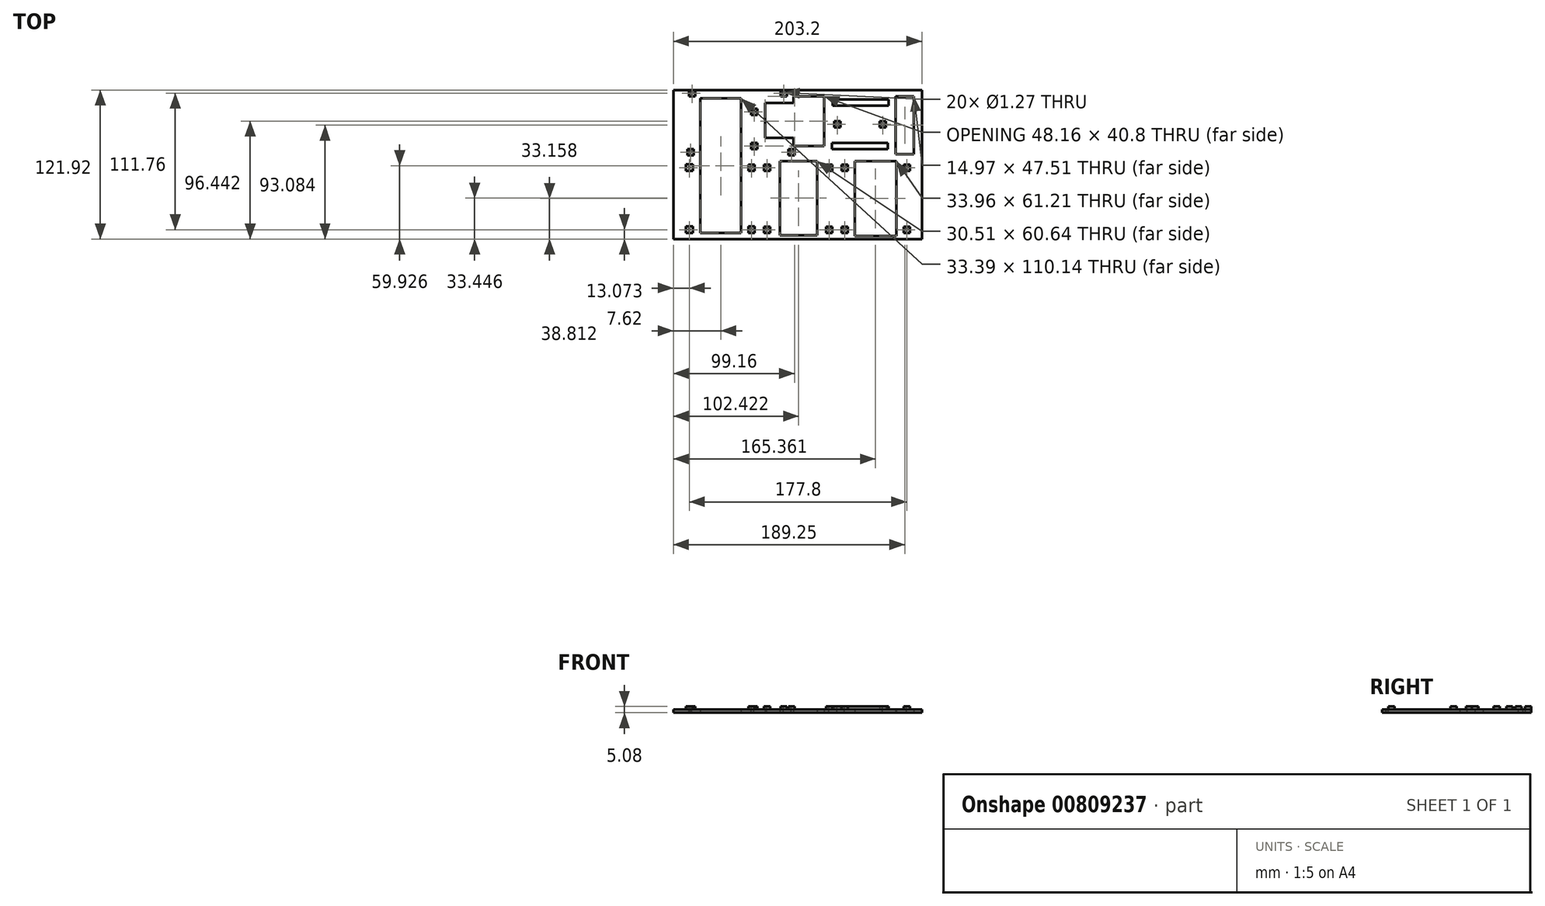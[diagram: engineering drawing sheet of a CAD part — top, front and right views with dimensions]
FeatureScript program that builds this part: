
annotation { "Feature Type Name" : "Feature", "Feature Type Description" : "" }
export const myFeature = defineFeature(function(context is Context, id is Id, definition is map)
    precondition{}
    {
        {
            var Q0;
            Q0=qCreatedBy(makeId("Top.planeOp"),FACE);
            var sketch = newSketch(context, id + "F0", { "sketchPlane" : qUnion([Q0])});
            skLineSegment(sketch, "E0.bottom", {"start": v(101.6, 60.96) * mm, "end": v(-101.6, 60.96) * mm});
            skLineSegment(sketch, "E0.top", {"start": v(101.6, -60.96) * mm, "end": v(-101.6, -60.96) * mm});
            skLineSegment(sketch, "E0.left", {"start": v(101.6, 60.96) * mm, "end": v(101.6, -60.96) * mm});
            skLineSegment(sketch, "E0.right", {"start": v(-101.6, 60.96) * mm, "end": v(-101.6, -60.96) * mm});
            skPoint(sketch, "E0.middle", {"position": v(0, 0) * mm});
            skLineSegment(sketch, "E1.bottom", {"start": v(-8.9, 55.88) * mm, "end": v(-13.97, 55.88) * mm});
            skLineSegment(sketch, "E1.top", {"start": v(-8.9, 60.96) * mm, "end": v(-13.97, 60.96) * mm});
            skLineSegment(sketch, "E1.left", {"start": v(-8.9, 55.88) * mm, "end": v(-8.9, 60.96) * mm});
            skLineSegment(sketch, "E1.right", {"start": v(-13.97, 55.88) * mm, "end": v(-13.97, 60.96) * mm});
            skPoint(sketch, "E1.middle", {"position": v(-11.43, 58.42) * mm});
            skLineSegment(sketch, "E2.bottom", {"start": v(-83.82, 55.88) * mm, "end": v(-88.9, 55.88) * mm});
            skLineSegment(sketch, "E2.top", {"start": v(-83.82, 60.96) * mm, "end": v(-88.9, 60.96) * mm});
            skLineSegment(sketch, "E2.left", {"start": v(-83.82, 55.88) * mm, "end": v(-83.82, 60.96) * mm});
            skLineSegment(sketch, "E2.right", {"start": v(-88.9, 55.88) * mm, "end": v(-88.9, 60.96) * mm});
            skPoint(sketch, "E2.middle", {"position": v(-86.36, 58.42) * mm});
            skLineSegment(sketch, "E3.bottom", {"start": v(-85.1, 7.62) * mm, "end": v(-90.17, 7.62) * mm});
            skLineSegment(sketch, "E3.top", {"start": v(-85.1, 12.7) * mm, "end": v(-90.17, 12.7) * mm});
            skLineSegment(sketch, "E3.left", {"start": v(-85.1, 7.62) * mm, "end": v(-85.1, 12.7) * mm});
            skLineSegment(sketch, "E3.right", {"start": v(-90.17, 7.62) * mm, "end": v(-90.17, 12.7) * mm});
            skPoint(sketch, "E3.middle", {"position": v(-87.63, 10.16) * mm});
            skLineSegment(sketch, "E4.bottom", {"start": v(-2.54, 7.62) * mm, "end": v(-7.62, 7.62) * mm});
            skLineSegment(sketch, "E4.top", {"start": v(-2.54, 12.7) * mm, "end": v(-7.62, 12.7) * mm});
            skLineSegment(sketch, "E4.left", {"start": v(-2.54, 7.62) * mm, "end": v(-2.54, 12.7) * mm});
            skLineSegment(sketch, "E4.right", {"start": v(-7.62, 7.62) * mm, "end": v(-7.62, 12.7) * mm});
            skPoint(sketch, "E4.middle", {"position": v(-5.08, 10.16) * mm});
            skLineSegment(sketch, "E5.bottom", {"start": v(-33.02, 40.64) * mm, "end": v(-38.1, 40.64) * mm});
            skLineSegment(sketch, "E5.top", {"start": v(-33.02, 45.72) * mm, "end": v(-38.1, 45.72) * mm});
            skLineSegment(sketch, "E5.left", {"start": v(-33.02, 40.64) * mm, "end": v(-33.02, 45.72) * mm});
            skLineSegment(sketch, "E5.right", {"start": v(-38.1, 40.64) * mm, "end": v(-38.1, 45.72) * mm});
            skPoint(sketch, "E5.middle", {"position": v(-35.56, 43.18) * mm});
            skLineSegment(sketch, "E6.bottom", {"start": v(-33.02, 12.7) * mm, "end": v(-38.1, 12.7) * mm});
            skLineSegment(sketch, "E6.top", {"start": v(-33.02, 17.78) * mm, "end": v(-38.1, 17.78) * mm});
            skLineSegment(sketch, "E6.left", {"start": v(-33.02, 12.7) * mm, "end": v(-33.02, 17.78) * mm});
            skLineSegment(sketch, "E6.right", {"start": v(-38.1, 12.7) * mm, "end": v(-38.1, 17.78) * mm});
            skPoint(sketch, "E6.middle", {"position": v(-35.56, 15.24) * mm});
            skPoint(sketch, "E7.middle", {"position": v(-88.53, -53.34) * mm});
            skLineSegment(sketch, "E8.bottom", {"start": v(-85.61, -5.1) * mm, "end": v(-91.44, -5.1) * mm});
            skLineSegment(sketch, "E8.top", {"start": v(-85.61, 0.02) * mm, "end": v(-91.44, 0.02) * mm});
            skLineSegment(sketch, "E8.left", {"start": v(-85.61, -5.1) * mm, "end": v(-85.61, 0.02) * mm});
            skLineSegment(sketch, "E8.right", {"start": v(-91.44, -5.1) * mm, "end": v(-91.44, 0.02) * mm});
            skPoint(sketch, "E8.middle", {"position": v(-88.53, -2.54) * mm});
            skLineSegment(sketch, "E9.bottom", {"start": v(-35.19, 0) * mm, "end": v(-40.27, 0) * mm});
            skLineSegment(sketch, "E9.top", {"start": v(-35.19, -5.08) * mm, "end": v(-40.27, -5.08) * mm});
            skLineSegment(sketch, "E9.left", {"start": v(-35.19, 0) * mm, "end": v(-35.19, -5.08) * mm});
            skLineSegment(sketch, "E9.right", {"start": v(-40.27, 0) * mm, "end": v(-40.27, -5.08) * mm});
            skPoint(sketch, "E9.middle", {"position": v(-37.73, -2.54) * mm});
            skLineSegment(sketch, "E10.bottom", {"start": v(-40.27, -50.78) * mm, "end": v(-35.19, -50.78) * mm});
            skLineSegment(sketch, "E10.top", {"start": v(-40.27, -55.9) * mm, "end": v(-35.19, -55.9) * mm});
            skLineSegment(sketch, "E10.left", {"start": v(-40.27, -50.78) * mm, "end": v(-40.27, -55.9) * mm});
            skLineSegment(sketch, "E10.right", {"start": v(-35.19, -50.78) * mm, "end": v(-35.19, -55.9) * mm});
            skPoint(sketch, "E10.middle", {"position": v(-37.73, -53.34) * mm});
            skLineSegment(sketch, "E11.bottom", {"start": v(-85.61, -50.78) * mm, "end": v(-91.44, -50.75) * mm});
            skLineSegment(sketch, "E11.left", {"start": v(-85.61, -50.78) * mm, "end": v(-85.61, -55.93) * mm});
            skLineSegment(sketch, "E11.right", {"start": v(-91.44, -50.75) * mm, "end": v(-91.44, -55.9) * mm});
            skLineSegment(sketch, "E12", {"start": v(-91.44, -55.9) * mm, "end": v(-85.61, -55.93) * mm});
            skLineSegment(sketch, "E13.bottom", {"start": v(-22.49, -55.88) * mm, "end": v(-27.57, -55.88) * mm});
            skLineSegment(sketch, "E13.top", {"start": v(-22.49, -50.8) * mm, "end": v(-27.57, -50.8) * mm});
            skLineSegment(sketch, "E13.left", {"start": v(-22.49, -55.88) * mm, "end": v(-22.49, -50.8) * mm});
            skLineSegment(sketch, "E13.right", {"start": v(-27.57, -55.88) * mm, "end": v(-27.57, -50.8) * mm});
            skPoint(sketch, "E13.middle", {"position": v(-25.03, -53.34) * mm});
            skLineSegment(sketch, "E14.bottom", {"start": v(28.31, -50.8) * mm, "end": v(23.23, -50.8) * mm});
            skLineSegment(sketch, "E14.top", {"start": v(28.31, -55.88) * mm, "end": v(23.23, -55.88) * mm});
            skLineSegment(sketch, "E14.left", {"start": v(28.31, -50.8) * mm, "end": v(28.31, -55.88) * mm});
            skLineSegment(sketch, "E14.right", {"start": v(23.23, -50.8) * mm, "end": v(23.23, -55.88) * mm});
            skPoint(sketch, "E14.middle", {"position": v(25.77, -53.34) * mm});
            skLineSegment(sketch, "E15.bottom", {"start": v(23.23, -5.08) * mm, "end": v(28.31, -5.08) * mm});
            skLineSegment(sketch, "E15.top", {"start": v(23.23, 0) * mm, "end": v(28.31, 0) * mm});
            skLineSegment(sketch, "E15.left", {"start": v(23.23, -5.08) * mm, "end": v(23.23, 0) * mm});
            skLineSegment(sketch, "E15.right", {"start": v(28.31, -5.08) * mm, "end": v(28.31, 0) * mm});
            skPoint(sketch, "E15.middle", {"position": v(25.77, -2.54) * mm});
            skLineSegment(sketch, "E16.bottom", {"start": v(-27.57, -5.08) * mm, "end": v(-22.49, -5.08) * mm});
            skLineSegment(sketch, "E16.top", {"start": v(-27.57, 0) * mm, "end": v(-22.49, 0) * mm});
            skLineSegment(sketch, "E16.left", {"start": v(-27.57, -5.08) * mm, "end": v(-27.57, 0) * mm});
            skLineSegment(sketch, "E16.right", {"start": v(-22.49, -5.08) * mm, "end": v(-22.49, 0) * mm});
            skPoint(sketch, "E16.middle", {"position": v(-25.03, -2.54) * mm});
            skPoint(sketch, "E16.middle.positionSnap0", {"position": v(-25.03, -50.8) * mm});
            skPoint(sketch, "E16.centerSnap0", {"position": v(-25.03, -50.8) * mm});
            skLineSegment(sketch, "E17.bottom", {"start": v(41.01, 0) * mm, "end": v(35.93, 0) * mm});
            skLineSegment(sketch, "E17.top", {"start": v(41.01, -5.08) * mm, "end": v(35.93, -5.08) * mm});
            skLineSegment(sketch, "E17.left", {"start": v(41.01, 0) * mm, "end": v(41.01, -5.08) * mm});
            skLineSegment(sketch, "E17.right", {"start": v(35.93, 0) * mm, "end": v(35.93, -5.08) * mm});
            skPoint(sketch, "E17.middle", {"position": v(38.47, -2.54) * mm});
            skLineSegment(sketch, "E18.bottom", {"start": v(91.81, 0) * mm, "end": v(86.73, 0) * mm});
            skLineSegment(sketch, "E18.top", {"start": v(91.81, -5.08) * mm, "end": v(86.73, -5.08) * mm});
            skLineSegment(sketch, "E18.left", {"start": v(91.81, 0) * mm, "end": v(91.81, -5.08) * mm});
            skLineSegment(sketch, "E18.right", {"start": v(86.73, 0) * mm, "end": v(86.73, -5.08) * mm});
            skPoint(sketch, "E18.middle", {"position": v(89.27, -2.54) * mm});
            skLineSegment(sketch, "E19.bottom", {"start": v(41.01, -50.8) * mm, "end": v(35.93, -50.8) * mm});
            skLineSegment(sketch, "E19.top", {"start": v(41.01, -55.88) * mm, "end": v(35.93, -55.88) * mm});
            skLineSegment(sketch, "E19.left", {"start": v(41.01, -50.8) * mm, "end": v(41.01, -55.88) * mm});
            skLineSegment(sketch, "E19.right", {"start": v(35.93, -50.8) * mm, "end": v(35.93, -55.88) * mm});
            skPoint(sketch, "E19.middle", {"position": v(38.47, -53.34) * mm});
            skLineSegment(sketch, "E20.bottom", {"start": v(86.73, -50.8) * mm, "end": v(91.81, -50.8) * mm});
            skLineSegment(sketch, "E20.top", {"start": v(86.73, -55.88) * mm, "end": v(91.81, -55.88) * mm});
            skLineSegment(sketch, "E20.left", {"start": v(86.73, -50.8) * mm, "end": v(86.73, -55.88) * mm});
            skLineSegment(sketch, "E20.right", {"start": v(91.81, -50.8) * mm, "end": v(91.81, -55.88) * mm});
            skPoint(sketch, "E20.middle", {"position": v(89.27, -53.34) * mm});
            skLineSegment(sketch, "E21.bottom", {"start": v(35.02, 30.3) * mm, "end": v(29.94, 30.3) * mm});
            skLineSegment(sketch, "E21.top", {"start": v(35.02, 35.38) * mm, "end": v(29.94, 35.38) * mm});
            skLineSegment(sketch, "E21.left", {"start": v(35.02, 30.3) * mm, "end": v(35.02, 35.38) * mm});
            skLineSegment(sketch, "E21.right", {"start": v(29.94, 30.3) * mm, "end": v(29.94, 35.38) * mm});
            skPoint(sketch, "E21.middle", {"position": v(32.48, 32.84) * mm});
            skLineSegment(sketch, "E22.bottom", {"start": v(72.1, 35.38) * mm, "end": v(67.02, 35.38) * mm});
            skLineSegment(sketch, "E22.top", {"start": v(72.1, 30.3) * mm, "end": v(67.02, 30.3) * mm});
            skLineSegment(sketch, "E22.left", {"start": v(72.1, 35.38) * mm, "end": v(72.1, 30.3) * mm});
            skLineSegment(sketch, "E22.right", {"start": v(67.02, 35.38) * mm, "end": v(67.02, 30.3) * mm});
            skPoint(sketch, "E22.middle", {"position": v(69.56, 32.84) * mm});
            skLineSegment(sketch, "E23.bottom", {"start": v(74.44, 53.16) * mm, "end": v(28.72, 53.16) * mm});
            skLineSegment(sketch, "E23.top", {"start": v(74.44, 48.08) * mm, "end": v(28.72, 48.08) * mm});
            skLineSegment(sketch, "E23.left", {"start": v(74.44, 53.16) * mm, "end": v(74.44, 48.08) * mm});
            skLineSegment(sketch, "E23.right", {"start": v(28.72, 53.16) * mm, "end": v(28.72, 48.08) * mm});
            skPoint(sketch, "E23.middle", {"position": v(51.58, 50.62) * mm});
            skLineSegment(sketch, "E24.bottom", {"start": v(73.88, 17.6) * mm, "end": v(28.16, 17.6) * mm});
            skLineSegment(sketch, "E24.top", {"start": v(73.88, 12.52) * mm, "end": v(28.16, 12.52) * mm});
            skLineSegment(sketch, "E24.left", {"start": v(73.88, 17.6) * mm, "end": v(73.88, 12.52) * mm});
            skLineSegment(sketch, "E24.right", {"start": v(28.16, 17.6) * mm, "end": v(28.16, 12.52) * mm});
            skPoint(sketch, "E24.middle", {"position": v(51.02, 15.06) * mm});
            skLineSegment(sketch, "E25.bottom", {"start": v(-79.48, 54.04) * mm, "end": v(-46.1, 54.04) * mm});
            skLineSegment(sketch, "E25.top", {"start": v(-79.48, -56.1) * mm, "end": v(-46.1, -56.1) * mm});
            skLineSegment(sketch, "E25.left", {"start": v(-79.48, 54.04) * mm, "end": v(-79.48, -56.1) * mm});
            skLineSegment(sketch, "E25.right", {"start": v(-46.1, 54.04) * mm, "end": v(-46.1, -56.1) * mm});
            skLineSegment(sketch, "E26.bottom", {"start": v(-14.43, 2.8) * mm, "end": v(16.08, 2.8) * mm});
            skLineSegment(sketch, "E26.top", {"start": v(-14.43, -57.83) * mm, "end": v(16.08, -57.83) * mm});
            skLineSegment(sketch, "E26.left", {"start": v(-14.43, 2.8) * mm, "end": v(-14.43, -57.83) * mm});
            skLineSegment(sketch, "E26.right", {"start": v(16.08, 2.8) * mm, "end": v(16.08, -57.83) * mm});
            skLineSegment(sketch, "E27.bottom", {"start": v(46.78, 2.8) * mm, "end": v(80.74, 2.8) * mm});
            skLineSegment(sketch, "E27.top", {"start": v(46.78, -58.4) * mm, "end": v(80.74, -58.4) * mm});
            skLineSegment(sketch, "E27.left", {"start": v(46.78, 2.8) * mm, "end": v(46.78, -58.4) * mm});
            skLineSegment(sketch, "E27.right", {"start": v(80.74, 2.8) * mm, "end": v(80.74, -58.4) * mm});
            skLineSegment(sketch, "E28.bottom", {"start": v(80.17, 55.88) * mm, "end": v(95.13, 55.88) * mm});
            skLineSegment(sketch, "E28.top", {"start": v(80.17, 8.37) * mm, "end": v(95.13, 8.37) * mm});
            skLineSegment(sketch, "E28.left", {"start": v(80.17, 55.88) * mm, "end": v(80.17, 8.37) * mm});
            skLineSegment(sketch, "E28.right", {"start": v(95.13, 55.88) * mm, "end": v(95.13, 8.37) * mm});
            skLineSegment(sketch, "E29.bottom", {"start": v(-3.5, 55.88) * mm, "end": v(21.64, 55.88) * mm});
            skLineSegment(sketch, "E29.top", {"start": v(-3.5, 15.08) * mm, "end": v(21.64, 15.08) * mm});
            skLineSegment(sketch, "E29.left", {"start": v(-3.5, 55.88) * mm, "end": v(-3.5, 15.08) * mm});
            skLineSegment(sketch, "E29.right", {"start": v(21.64, 55.88) * mm, "end": v(21.64, 15.08) * mm});
            skLineSegment(sketch, "E30.bottom", {"start": v(-26.52, 50.4) * mm, "end": v(-3.5, 50.4) * mm});
            skLineSegment(sketch, "E30.top", {"start": v(-26.52, 21.6) * mm, "end": v(-3.5, 21.6) * mm});
            skLineSegment(sketch, "E30.left", {"start": v(-26.52, 50.4) * mm, "end": v(-26.52, 21.6) * mm});
            skLineSegment(sketch, "E30.right", {"start": v(-3.5, 50.4) * mm, "end": v(-3.5, 21.6) * mm});
            skSolve(sketch);
        }
        {
            var Q0;
            Q0=makeQuery(id+"F0.imprint","IMPRINT",FACE,{"disambiguationData":[TD([[makeQuery(id+"F0.imprint","IMPRINT",EDGE,{"derivedFrom":sQuery(id+"F0.wireOp",EDGE,"E0.top")}),-1.0]])]});
            extrude(context, id + "F1", {"entities" : qUnion([Q0]), "depth" : 2.54 * mm, "offsetDistance" : 25.4 * mm});
        }
        {
            var Q0;
            Q0=makeQuery(id+"F0.imprint","IMPRINT",FACE,{"disambiguationData":[TD([[makeQuery(id+"F0.imprint","IMPRINT",EDGE,{"derivedFrom":sQuery(id+"F0.wireOp",EDGE,"E2.bottom")}),-1.0]])]});
            var Q1;
            Q1=makeQuery(id+"F0.imprint","IMPRINT",FACE,{"disambiguationData":[TD([[makeQuery(id+"F0.imprint","IMPRINT",EDGE,{"derivedFrom":sQuery(id+"F0.wireOp",EDGE,"E5.bottom")}),-1.0]])]});
            var Q2;
            Q2=makeQuery(id+"F0.imprint","IMPRINT",FACE,{"disambiguationData":[TD([[makeQuery(id+"F0.imprint","IMPRINT",EDGE,{"derivedFrom":sQuery(id+"F0.wireOp",EDGE,"E1.bottom")}),-1.0]])]});
            var Q3;
            Q3=makeQuery(id+"F0.imprint","IMPRINT",FACE,{"disambiguationData":[TD([[makeQuery(id+"F0.imprint","IMPRINT",EDGE,{"derivedFrom":sQuery(id+"F0.wireOp",EDGE,"E6.bottom")}),-1.0]])]});
            var Q4;
            Q4=makeQuery(id+"F0.imprint","IMPRINT",FACE,{"disambiguationData":[TD([[makeQuery(id+"F0.imprint","IMPRINT",EDGE,{"derivedFrom":sQuery(id+"F0.wireOp",EDGE,"E4.bottom")}),-1.0]])]});
            var Q5;
            Q5=makeQuery(id+"F0.imprint","IMPRINT",FACE,{"disambiguationData":[TD([[makeQuery(id+"F0.imprint","IMPRINT",EDGE,{"derivedFrom":sQuery(id+"F0.wireOp",EDGE,"E3.bottom")}),-1.0]])]});
            var Q6;
            Q6=makeQuery(id+"F0.imprint","IMPRINT",FACE,{"disambiguationData":[TD([[makeQuery(id+"F0.imprint","IMPRINT",EDGE,{"derivedFrom":sQuery(id+"F0.wireOp",EDGE,"E8.bottom")}),-1.0]])]});
            var Q7;
            Q7=makeQuery(id+"F0.imprint","IMPRINT",FACE,{"disambiguationData":[TD([[makeQuery(id+"F0.imprint","IMPRINT",EDGE,{"derivedFrom":sQuery(id+"F0.wireOp",EDGE,"E9.bottom")}),1.0]])]});
            var Q8;
            Q8=makeQuery(id+"F0.imprint","IMPRINT",FACE,{"disambiguationData":[TD([[makeQuery(id+"F0.imprint","IMPRINT",EDGE,{"derivedFrom":sQuery(id+"F0.wireOp",EDGE,"E10.bottom")}),-1.0]])]});
            var Q9;
            {var subQ4=sQuery(id+"F0.wireOp",EDGE,"E7.top");Q9=makeQuery(id+"F0.imprint","IMPRINT",FACE,{"disambiguationData":[TD([[makeQuery(id+"F0.imprint","IMPRINT",EDGE,{"derivedFrom":subQ4}),-1.0]])]});}
            var Q10;
            Q10=makeQuery(id+"F0.imprint","IMPRINT",FACE,{"disambiguationData":[TD([[makeQuery(id+"F0.imprint","IMPRINT",EDGE,{"derivedFrom":sQuery(id+"F0.wireOp",EDGE,"E16.bottom")}),1.0]])]});
            var Q11;
            Q11=makeQuery(id+"F0.imprint","IMPRINT",FACE,{"disambiguationData":[TD([[makeQuery(id+"F0.imprint","IMPRINT",EDGE,{"derivedFrom":sQuery(id+"F0.wireOp",EDGE,"E15.bottom")}),1.0]])]});
            var Q12;
            Q12=makeQuery(id+"F0.imprint","IMPRINT",FACE,{"disambiguationData":[TD([[makeQuery(id+"F0.imprint","IMPRINT",EDGE,{"derivedFrom":sQuery(id+"F0.wireOp",EDGE,"E17.bottom")}),1.0]])]});
            var Q13;
            Q13=makeQuery(id+"F0.imprint","IMPRINT",FACE,{"disambiguationData":[TD([[makeQuery(id+"F0.imprint","IMPRINT",EDGE,{"derivedFrom":sQuery(id+"F0.wireOp",EDGE,"E18.bottom")}),1.0]])]});
            var Q14;
            Q14=makeQuery(id+"F0.imprint","IMPRINT",FACE,{"disambiguationData":[TD([[makeQuery(id+"F0.imprint","IMPRINT",EDGE,{"derivedFrom":sQuery(id+"F0.wireOp",EDGE,"E20.bottom")}),-1.0]])]});
            var Q15;
            Q15=makeQuery(id+"F0.imprint","IMPRINT",FACE,{"disambiguationData":[TD([[makeQuery(id+"F0.imprint","IMPRINT",EDGE,{"derivedFrom":sQuery(id+"F0.wireOp",EDGE,"E19.bottom")}),1.0]])]});
            var Q16;
            Q16=makeQuery(id+"F0.imprint","IMPRINT",FACE,{"disambiguationData":[TD([[makeQuery(id+"F0.imprint","IMPRINT",EDGE,{"derivedFrom":sQuery(id+"F0.wireOp",EDGE,"E14.bottom")}),1.0]])]});
            var Q17;
            Q17=makeQuery(id+"F0.imprint","IMPRINT",FACE,{"disambiguationData":[TD([[makeQuery(id+"F0.imprint","IMPRINT",EDGE,{"derivedFrom":sQuery(id+"F0.wireOp",EDGE,"E13.bottom")}),-1.0]])]});
            var Q18;
            Q18=makeQuery(id+"F0.imprint","IMPRINT",FACE,{"disambiguationData":[TD([[makeQuery(id+"F0.imprint","IMPRINT",EDGE,{"derivedFrom":sQuery(id+"F0.wireOp",EDGE,"E11.bottom")}),1.0]])]});
            var Q19;
            Q19=makeQuery(id+"F0.imprint","IMPRINT",FACE,{"disambiguationData":[TD([[makeQuery(id+"F0.imprint","IMPRINT",EDGE,{"derivedFrom":sQuery(id+"F0.wireOp",EDGE,"E21.bottom")}),-1.0]])]});
            var Q20;
            Q20=makeQuery(id+"F0.imprint","IMPRINT",FACE,{"disambiguationData":[TD([[makeQuery(id+"F0.imprint","IMPRINT",EDGE,{"derivedFrom":sQuery(id+"F0.wireOp",EDGE,"E24.bottom")}),1.0]])]});
            var Q21;
            Q21=makeQuery(id+"F0.imprint","IMPRINT",FACE,{"disambiguationData":[TD([[makeQuery(id+"F0.imprint","IMPRINT",EDGE,{"derivedFrom":sQuery(id+"F0.wireOp",EDGE,"E22.bottom")}),1.0]])]});
            var Q22;
            Q22=makeQuery(id+"F0.imprint","IMPRINT",FACE,{"disambiguationData":[TD([[makeQuery(id+"F0.imprint","IMPRINT",EDGE,{"derivedFrom":sQuery(id+"F0.wireOp",EDGE,"E23.bottom")}),1.0]])]});
            extrude(context, id + "F2", {"entities" : qUnion([Q0, Q1, Q2, Q3, Q4, Q5, Q6, Q7, Q8, Q9, Q10, Q11, Q12, Q13, Q14, Q15, Q16, Q17, Q18, Q19, Q20, Q21, Q22]), "operationType" : NewBodyOperationType.ADD, "depth" : 5.08 * mm, "offsetDistance" : 25.4 * mm});
        }
        {
            var Q0;
            Q0=makeQuery(id+"F1.opExtrude","CAP_FACE",FACE,{"disambiguationData":[OSD([sQuery(id+"F0.wireOp",EDGE,"E0.bottom"),sQuery(id+"F0.wireOp",EDGE,"E0.top"),sQuery(id+"F0.wireOp",EDGE,"E0.left"),sQuery(id+"F0.wireOp",EDGE,"E0.right"),sQuery(id+"F0.wireOp",EDGE,"E1.bottom"),sQuery(id+"F0.wireOp",EDGE,"E1.left"),sQuery(id+"F0.wireOp",EDGE,"E1.right"),sQuery(id+"F0.wireOp",EDGE,"E2.bottom"),sQuery(id+"F0.wireOp",EDGE,"E2.left"),sQuery(id+"F0.wireOp",EDGE,"E2.right"),sQuery(id+"F0.wireOp",EDGE,"E3.bottom"),sQuery(id+"F0.wireOp",EDGE,"E3.top"),sQuery(id+"F0.wireOp",EDGE,"E3.left"),sQuery(id+"F0.wireOp",EDGE,"E3.right"),sQuery(id+"F0.wireOp",EDGE,"E4.bottom"),sQuery(id+"F0.wireOp",EDGE,"E4.top"),sQuery(id+"F0.wireOp",EDGE,"E4.left"),sQuery(id+"F0.wireOp",EDGE,"E4.right"),sQuery(id+"F0.wireOp",EDGE,"E5.bottom"),sQuery(id+"F0.wireOp",EDGE,"E5.top"),sQuery(id+"F0.wireOp",EDGE,"E5.left"),sQuery(id+"F0.wireOp",EDGE,"E5.right"),sQuery(id+"F0.wireOp",EDGE,"E6.bottom"),sQuery(id+"F0.wireOp",EDGE,"E6.top"),sQuery(id+"F0.wireOp",EDGE,"E6.left"),sQuery(id+"F0.wireOp",EDGE,"E6.right"),sQuery(id+"F0.wireOp",EDGE,"E7.bottom"),sQuery(id+"F0.wireOp",EDGE,"E7.top"),sQuery(id+"F0.wireOp",EDGE,"E7.left"),sQuery(id+"F0.wireOp",EDGE,"E7.right"),sQuery(id+"F0.wireOp",EDGE,"E8.bottom"),sQuery(id+"F0.wireOp",EDGE,"E8.top"),sQuery(id+"F0.wireOp",EDGE,"E8.left"),sQuery(id+"F0.wireOp",EDGE,"E8.right"),sQuery(id+"F0.wireOp",EDGE,"E9.bottom"),sQuery(id+"F0.wireOp",EDGE,"E9.top"),sQuery(id+"F0.wireOp",EDGE,"E9.left"),sQuery(id+"F0.wireOp",EDGE,"E9.right"),sQuery(id+"F0.wireOp",EDGE,"E10.bottom"),sQuery(id+"F0.wireOp",EDGE,"E10.top"),sQuery(id+"F0.wireOp",EDGE,"E10.left"),sQuery(id+"F0.wireOp",EDGE,"E10.right")])],"isStart":false});
            var sketch = newSketch(context, id + "F3", { "sketchPlane" : qUnion([Q0])});
            skPoint(sketch, "E31", {"position": v(0, 30.48) * mm});
            skPoint(sketch, "E32", {"position": v(0, -30.48) * mm});
            skSolve(sketch);
        }
        {
            var Q0;
            Q0=sQuery(id+"F3.wireOp",VERTEX,"E31");
            var Q1;
            Q1=sQuery(id+"F3.wireOp",VERTEX,"E32");
            var Q2;
            Q2=makeQuery(id+"F1.opExtrude","SWEPT_BODY",BODY,{"disambiguationData":[OSD([sQuery(id+"F0.wireOp",EDGE,"E0.bottom"),sQuery(id+"F0.wireOp",EDGE,"E0.top"),sQuery(id+"F0.wireOp",EDGE,"E0.left"),sQuery(id+"F0.wireOp",EDGE,"E0.right"),sQuery(id+"F0.wireOp",EDGE,"E1.bottom"),sQuery(id+"F0.wireOp",EDGE,"E1.left"),sQuery(id+"F0.wireOp",EDGE,"E1.right"),sQuery(id+"F0.wireOp",EDGE,"E2.bottom"),sQuery(id+"F0.wireOp",EDGE,"E2.left"),sQuery(id+"F0.wireOp",EDGE,"E2.right"),sQuery(id+"F0.wireOp",EDGE,"E3.bottom"),sQuery(id+"F0.wireOp",EDGE,"E3.top"),sQuery(id+"F0.wireOp",EDGE,"E3.left"),sQuery(id+"F0.wireOp",EDGE,"E3.right"),sQuery(id+"F0.wireOp",EDGE,"E4.bottom"),sQuery(id+"F0.wireOp",EDGE,"E4.top"),sQuery(id+"F0.wireOp",EDGE,"E4.left"),sQuery(id+"F0.wireOp",EDGE,"E4.right"),sQuery(id+"F0.wireOp",EDGE,"E5.bottom"),sQuery(id+"F0.wireOp",EDGE,"E5.top"),sQuery(id+"F0.wireOp",EDGE,"E5.left"),sQuery(id+"F0.wireOp",EDGE,"E5.right"),sQuery(id+"F0.wireOp",EDGE,"E6.bottom"),sQuery(id+"F0.wireOp",EDGE,"E6.top"),sQuery(id+"F0.wireOp",EDGE,"E6.left"),sQuery(id+"F0.wireOp",EDGE,"E6.right"),sQuery(id+"F0.wireOp",EDGE,"E7.bottom"),sQuery(id+"F0.wireOp",EDGE,"E7.top"),sQuery(id+"F0.wireOp",EDGE,"E7.left"),sQuery(id+"F0.wireOp",EDGE,"E7.right"),sQuery(id+"F0.wireOp",EDGE,"E8.bottom"),sQuery(id+"F0.wireOp",EDGE,"E8.top"),sQuery(id+"F0.wireOp",EDGE,"E8.left"),sQuery(id+"F0.wireOp",EDGE,"E8.right"),sQuery(id+"F0.wireOp",EDGE,"E9.bottom"),sQuery(id+"F0.wireOp",EDGE,"E9.top"),sQuery(id+"F0.wireOp",EDGE,"E9.left"),sQuery(id+"F0.wireOp",EDGE,"E9.right"),sQuery(id+"F0.wireOp",EDGE,"E10.bottom"),sQuery(id+"F0.wireOp",EDGE,"E10.top"),sQuery(id+"F0.wireOp",EDGE,"E10.left"),sQuery(id+"F0.wireOp",EDGE,"E10.right")])]});
            hole(context, id + "F4", {"style" : HoleStyle.C_SINK, "endStyle" : HoleEndStyle.THROUGH, "holeDiameter" : 3.17 * mm, "cSinkDiameter" : 6.86 * mm, "cSinkAngle" : 90 * degree, "majorDiameter" : 6.35 * mm, "isTappedThrough" : true, "tappedDepth" : 12.7 * mm, "tapClearance" : 3, "locations" : qUnion([Q0, Q1]), "scope" : qUnion([Q2])});
        }
        {
            var Q0;
            Q0=sQuery(id+"F0.wireOp",VERTEX,"E16.middle");
            var Q1;
            Q1=sQuery(id+"F0.wireOp",VERTEX,"E9.middle");
            var Q2;
            Q2=sQuery(id+"F0.wireOp",VERTEX,"E15.middle");
            var Q3;
            Q3=sQuery(id+"F0.wireOp",VERTEX,"E17.middle");
            var Q4;
            Q4=sQuery(id+"F0.wireOp",VERTEX,"E18.middle");
            var Q5;
            Q5=sQuery(id+"F0.wireOp",VERTEX,"E20.middle");
            var Q6;
            Q6=sQuery(id+"F0.wireOp",VERTEX,"E19.middle");
            var Q7;
            Q7=sQuery(id+"F0.wireOp",VERTEX,"E14.middle");
            var Q8;
            Q8=sQuery(id+"F0.wireOp",VERTEX,"E13.middle");
            var Q9;
            Q9=sQuery(id+"F0.wireOp",VERTEX,"E10.middle");
            var Q10;
            Q10=sQuery(id+"F0.wireOp",VERTEX,"E7.middle");
            var Q11;
            Q11=sQuery(id+"F0.wireOp",VERTEX,"E8.middle");
            var Q12;
            Q12=sQuery(id+"F0.wireOp",VERTEX,"E3.middle");
            var Q13;
            Q13=sQuery(id+"F0.wireOp",VERTEX,"E6.middle");
            var Q14;
            Q14=sQuery(id+"F0.wireOp",VERTEX,"E4.middle");
            var Q15;
            Q15=sQuery(id+"F0.wireOp",VERTEX,"E21.middle");
            var Q16;
            Q16=sQuery(id+"F0.wireOp",VERTEX,"E22.middle");
            var Q17;
            Q17=sQuery(id+"F0.wireOp",VERTEX,"E1.middle");
            var Q18;
            Q18=sQuery(id+"F0.wireOp",VERTEX,"E5.middle");
            var Q19;
            Q19=sQuery(id+"F0.wireOp",VERTEX,"E2.middle");
            var Q20;
            Q20=makeQuery(id+"F1.opExtrude","SWEPT_BODY",BODY,{"disambiguationData":[OSD([sQuery(id+"F0.wireOp",EDGE,"E0.bottom"),sQuery(id+"F0.wireOp",EDGE,"E0.top"),sQuery(id+"F0.wireOp",EDGE,"E0.left"),sQuery(id+"F0.wireOp",EDGE,"E0.right"),sQuery(id+"F0.wireOp",EDGE,"E1.bottom"),sQuery(id+"F0.wireOp",EDGE,"E1.left"),sQuery(id+"F0.wireOp",EDGE,"E1.right"),sQuery(id+"F0.wireOp",EDGE,"E2.bottom"),sQuery(id+"F0.wireOp",EDGE,"E2.left"),sQuery(id+"F0.wireOp",EDGE,"E2.right"),sQuery(id+"F0.wireOp",EDGE,"E3.bottom"),sQuery(id+"F0.wireOp",EDGE,"E3.top"),sQuery(id+"F0.wireOp",EDGE,"E3.left"),sQuery(id+"F0.wireOp",EDGE,"E3.right"),sQuery(id+"F0.wireOp",EDGE,"E4.bottom"),sQuery(id+"F0.wireOp",EDGE,"E4.top"),sQuery(id+"F0.wireOp",EDGE,"E4.left"),sQuery(id+"F0.wireOp",EDGE,"E4.right"),sQuery(id+"F0.wireOp",EDGE,"E5.bottom"),sQuery(id+"F0.wireOp",EDGE,"E5.top"),sQuery(id+"F0.wireOp",EDGE,"E5.left"),sQuery(id+"F0.wireOp",EDGE,"E5.right"),sQuery(id+"F0.wireOp",EDGE,"E6.bottom"),sQuery(id+"F0.wireOp",EDGE,"E6.top"),sQuery(id+"F0.wireOp",EDGE,"E6.left"),sQuery(id+"F0.wireOp",EDGE,"E6.right"),sQuery(id+"F0.wireOp",EDGE,"E8.bottom"),sQuery(id+"F0.wireOp",EDGE,"E8.top"),sQuery(id+"F0.wireOp",EDGE,"E8.left"),sQuery(id+"F0.wireOp",EDGE,"E8.right"),sQuery(id+"F0.wireOp",EDGE,"E9.bottom"),sQuery(id+"F0.wireOp",EDGE,"E9.top"),sQuery(id+"F0.wireOp",EDGE,"E9.left"),sQuery(id+"F0.wireOp",EDGE,"E9.right"),sQuery(id+"F0.wireOp",EDGE,"E10.bottom"),sQuery(id+"F0.wireOp",EDGE,"E10.top"),sQuery(id+"F0.wireOp",EDGE,"E10.left"),sQuery(id+"F0.wireOp",EDGE,"E10.right"),sQuery(id+"F0.wireOp",EDGE,"E11.bottom"),sQuery(id+"F0.wireOp",EDGE,"E11.left"),sQuery(id+"F0.wireOp",EDGE,"E11.right"),sQuery(id+"F0.wireOp",EDGE,"E12"),sQuery(id+"F0.wireOp",EDGE,"E13.bottom"),sQuery(id+"F0.wireOp",EDGE,"E13.top"),sQuery(id+"F0.wireOp",EDGE,"E13.left"),sQuery(id+"F0.wireOp",EDGE,"E13.right"),sQuery(id+"F0.wireOp",EDGE,"E14.bottom"),sQuery(id+"F0.wireOp",EDGE,"E14.top"),sQuery(id+"F0.wireOp",EDGE,"E14.left"),sQuery(id+"F0.wireOp",EDGE,"E14.right"),sQuery(id+"F0.wireOp",EDGE,"E15.bottom"),sQuery(id+"F0.wireOp",EDGE,"E15.top"),sQuery(id+"F0.wireOp",EDGE,"E15.left"),sQuery(id+"F0.wireOp",EDGE,"E15.right"),sQuery(id+"F0.wireOp",EDGE,"E16.bottom"),sQuery(id+"F0.wireOp",EDGE,"E16.top"),sQuery(id+"F0.wireOp",EDGE,"E16.left"),sQuery(id+"F0.wireOp",EDGE,"E16.right"),sQuery(id+"F0.wireOp",EDGE,"E17.bottom"),sQuery(id+"F0.wireOp",EDGE,"E17.top"),sQuery(id+"F0.wireOp",EDGE,"E17.left"),sQuery(id+"F0.wireOp",EDGE,"E17.right"),sQuery(id+"F0.wireOp",EDGE,"E18.bottom"),sQuery(id+"F0.wireOp",EDGE,"E18.top"),sQuery(id+"F0.wireOp",EDGE,"E18.left"),sQuery(id+"F0.wireOp",EDGE,"E18.right"),sQuery(id+"F0.wireOp",EDGE,"E19.bottom"),sQuery(id+"F0.wireOp",EDGE,"E19.top"),sQuery(id+"F0.wireOp",EDGE,"E19.left"),sQuery(id+"F0.wireOp",EDGE,"E19.right"),sQuery(id+"F0.wireOp",EDGE,"E20.bottom"),sQuery(id+"F0.wireOp",EDGE,"E20.top"),sQuery(id+"F0.wireOp",EDGE,"E20.left"),sQuery(id+"F0.wireOp",EDGE,"E20.right"),sQuery(id+"F0.wireOp",EDGE,"E21.bottom"),sQuery(id+"F0.wireOp",EDGE,"E21.top"),sQuery(id+"F0.wireOp",EDGE,"E21.left"),sQuery(id+"F0.wireOp",EDGE,"E21.right"),sQuery(id+"F0.wireOp",EDGE,"E22.bottom"),sQuery(id+"F0.wireOp",EDGE,"E22.top"),sQuery(id+"F0.wireOp",EDGE,"E22.left"),sQuery(id+"F0.wireOp",EDGE,"E22.right"),sQuery(id+"F0.wireOp",EDGE,"E23.bottom"),sQuery(id+"F0.wireOp",EDGE,"E23.top"),sQuery(id+"F0.wireOp",EDGE,"E23.left"),sQuery(id+"F0.wireOp",EDGE,"E23.right"),sQuery(id+"F0.wireOp",EDGE,"E24.bottom"),sQuery(id+"F0.wireOp",EDGE,"E24.top"),sQuery(id+"F0.wireOp",EDGE,"E24.left"),sQuery(id+"F0.wireOp",EDGE,"E24.right")])]});
            hole(context, id + "F5", {"style" : HoleStyle.SIMPLE, "endStyle" : HoleEndStyle.THROUGH, "oppositeDirection" : true, "holeDiameter" : 1.27 * mm, "majorDiameter" : 6.35 * mm, "isTappedThrough" : true, "tappedDepth" : 12.7 * mm, "tapClearance" : 3, "locations" : qUnion([Q0, Q1, Q2, Q3, Q4, Q5, Q6, Q7, Q8, Q9, Q10, Q11, Q12, Q13, Q14, Q15, Q16, Q17, Q18, Q19]), "scope" : qUnion([Q20])});
        }
    });
